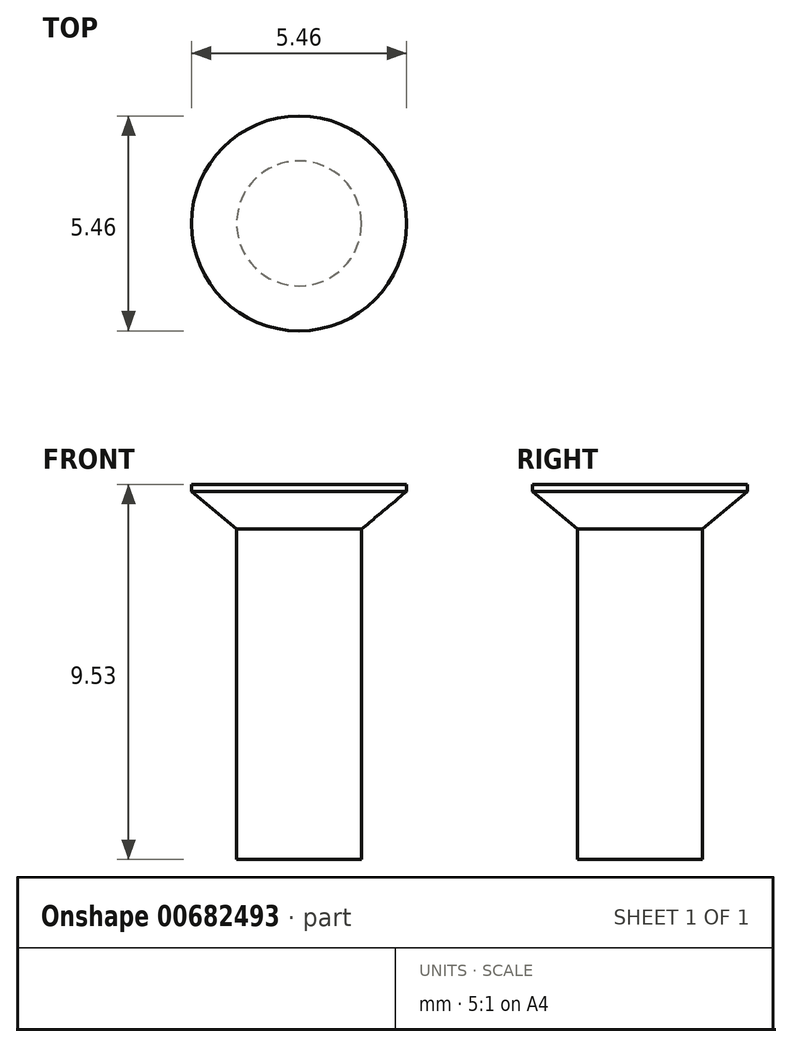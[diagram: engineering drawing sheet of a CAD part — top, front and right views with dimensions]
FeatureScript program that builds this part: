
annotation { "Feature Type Name" : "Feature", "Feature Type Description" : "" }
export const myFeature = defineFeature(function(context is Context, id is Id, definition is map)
    precondition{}
    {
        {
            var Q0;
            Q0=qCreatedBy(makeId("Front.planeOp"),FACE);
            var sketch = newSketch(context, id + "F0", { "sketchPlane" : qUnion([Q0])});
            skLineSegment(sketch, "E0", {"start": v(0, 0) * mm, "end": v(-2.73, 0) * mm});
            skLineSegment(sketch, "E1", {"start": v(-2.73, 0) * mm, "end": v(-2.73, -0.18) * mm});
            skLineSegment(sketch, "E2", {"start": v(-2.73, -0.18) * mm, "end": v(-1.59, -1.14) * mm});
            skLineSegment(sketch, "E3", {"start": v(-1.59, -1.14) * mm, "end": v(-1.59, -9.53) * mm});
            skLineSegment(sketch, "E4", {"start": v(-1.59, -9.53) * mm, "end": v(0, -9.53) * mm});
            skLineSegment(sketch, "E5", {"start": v(0, -9.53) * mm, "end": v(0, 0) * mm});
            skLineSegment(sketch, "E6", {"start": v(-2.73, -0.18) * mm, "end": v(0, -0.18) * mm, "construction": true});
            skLineSegment(sketch, "E7", {"start": v(-1.59, -1.14) * mm, "end": v(-1.59, -0.18) * mm, "construction": true});
            skLineSegment(sketch, "E8", {"start": v(0, 73.66) * mm, "end": v(0, -52.05) * mm, "construction": true});
            skSolve(sketch);
        }
        {
            var Q0;
            Q0=makeQuery(id+"F0.imprint","IMPRINT",FACE,{"disambiguationData":[TD([[makeQuery(id+"F0.imprint","IMPRINT",EDGE,{"derivedFrom":sQuery(id+"F0.wireOp",EDGE,"E0")}),1.0]])]});
            var Q1;
            Q1=sQuery(id+"F0.wireOp",EDGE,"E8");
            revolve(context, id + "F1", {"entities" : qUnion([Q0]), "axis" : qUnion([Q1]), "revolveType" : RevolveType.FULL});
        }
    });
